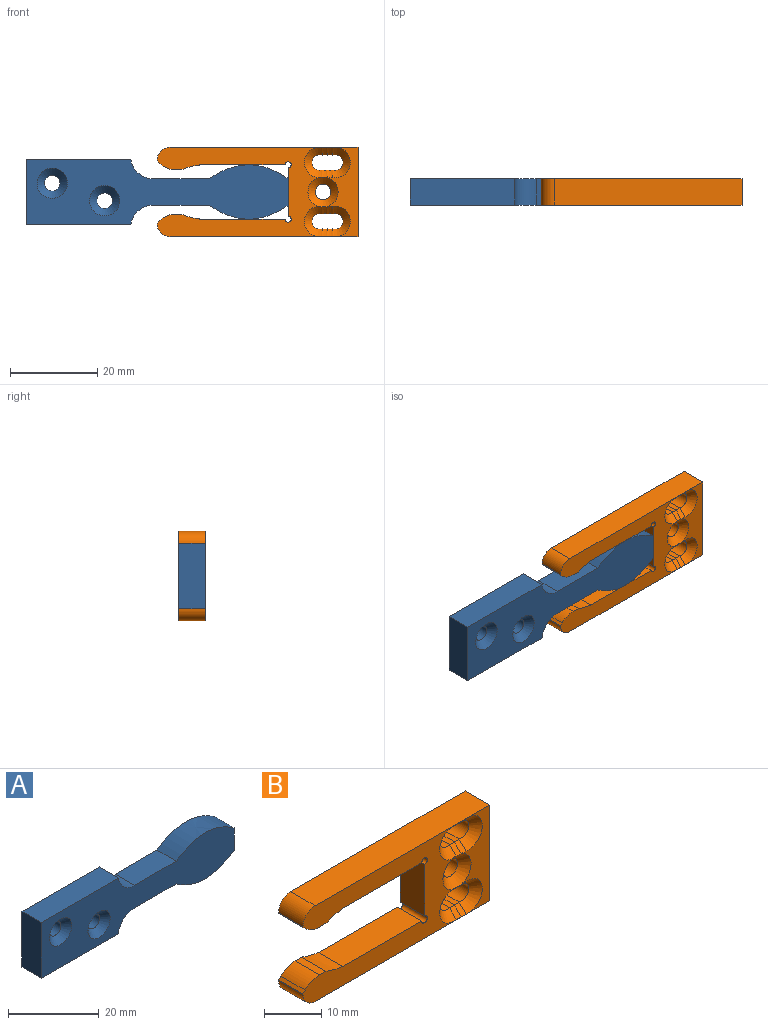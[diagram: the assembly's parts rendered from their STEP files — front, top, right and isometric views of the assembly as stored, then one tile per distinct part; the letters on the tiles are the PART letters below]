
ASSEMBLY  parts=2 mates=1
PART A: 16 faces, bbox 60x6x15 mm
  f0: plane 13.03x6mm, normal (0,0,-1), area 78.2mm2, adj f1,f8,f9,f10
  f1: extruded ~18x6mm, area 116.3mm2, adj f0,f2,f8,f9
  f2: plane 6.11x6mm, normal (1,0,0), area 36.7mm2, adj f1,f3,f8,f9
  f3: extruded ~18x6mm, area 116.3mm2, adj f2,f4,f8,f9
  f4: plane 13.03x6mm, normal (0,0,1), area 78.2mm2, adj f3,f8,f9,f11
  f5: plane 24x6mm, normal (0,0,1), area 144mm2, adj f6,f8,f9,f11
  f6: plane 15x6mm, normal (-1,0,0), area 90mm2, adj f5,f7,f8,f9
  f7: plane 24x6mm, normal (0,0,-1), area 144mm2, adj f6,f8,f9,f10
  f8: plane 60x15mm, normal (0,1,0), area 646.1mm2, adj f0,f1,f2,f3,f4,f5,f6,f7
  f9: plane 60x15mm, normal (0,-1,0), area 590.8mm2, adj f0,f1,f2,f3,f4,f5,f6,f7
  f10: cylinder r=5mm len=6mm, axis (0,-1,0), area 43.8mm2, adj f0,f7,f8,f9
  f11: cylinder r=5mm len=6mm, axis (0,-1,0), area 43.8mm2, adj f4,f5,f8,f9
  f12: cylinder r=1.8mm len=4.33mm, axis (0,-1,0), area 49mm2, adj f8,f13
  f13: cone r=1.8mm half-angle=45deg, axis (0,-1,0), area 39.1mm2, adj f9,f12
  f14: cylinder r=1.8mm len=4.33mm, axis (0,-1,0), area 49mm2, adj f8,f15
  f15: cone r=1.8mm half-angle=45deg, axis (0,-1,0), area 39.1mm2, adj f9,f14
PART B: 50 faces, bbox 46x6x20.4 mm
  f0: plane 46x20.43mm, normal (0,-1,0), area 409.2mm2, adj f1,f2,f4,f5,f6,f7,f8,f9
  f1: plane 6x0.06mm, normal (1,0,0), area 0.3mm2, adj f0,f3,f11,f16
  f2: plane 6x1.62mm, normal (0,0,1), area 9.7mm2, adj f0,f3,f16,f23
  f3: plane 46x20.43mm, normal (0,1,0), area 515.9mm2, adj f1,f2,f4,f5,f6,f7,f8,f9
  f4: plane 6x0.1mm, normal (-1,0,0), area 0.6mm2, adj f0,f3,f18,f21
  f5: plane 6x1.62mm, normal (0,0,-1), area 9.7mm2, adj f0,f3,f17,f22
  f6: plane 6x0.06mm, normal (1,0,0), area 0.3mm2, adj f0,f3,f7,f17
  f7: plane 19.5x6mm, normal (0,0,-1), area 117mm2, adj f0,f3,f6,f8
  f8: cylinder r=0.7mm len=6mm, axis (0,-1,0), area 19.8mm2, adj f0,f3,f7,f9
  f9: plane 11.04x6mm, normal (-1,0,0), area 66.2mm2, adj f0,f3,f8,f10
  f10: cylinder r=0.7mm len=6mm, axis (0,-1,0), area 19.8mm2, adj f0,f3,f9,f11
  f11: plane 19.5x6mm, normal (0,0,1), area 117mm2, adj f0,f1,f3,f10
  f12: plane 6x0.1mm, normal (-1,0,0), area 0.6mm2, adj f0,f3,f19,f20
  f13: plane 43x6mm, normal (0,0,-1), area 258mm2, adj f0,f3,f14,f19
  f14: plane 20.43x6mm, normal (1,0,0), area 122.6mm2, adj f0,f3,f13,f15
  f15: plane 43x6mm, normal (0,0,1), area 258mm2, adj f0,f3,f14,f18
  f16: extruded ~6x4.11mm, area 25.5mm2, adj f0,f1,f2,f3
  f17: extruded ~6x4.11mm, area 25.5mm2, adj f0,f3,f5,f6
  f18: cylinder r=3mm len=6mm, axis (0,-1,0), area 28.3mm2, adj f0,f3,f4,f15
  f19: cylinder r=3mm len=6mm, axis (0,-1,0), area 28.3mm2, adj f0,f3,f12,f13
  f20: plane 6x0.54mm, normal (-0.71,0,0.71), area 4.5mm2, adj f0,f3,f12,f23
  f21: plane 6x0.54mm, normal (-0.71,0,-0.71), area 4.5mm2, adj f0,f3,f4,f22
  f22: cylinder r=5mm len=6mm, axis (0,1,0), area 23.6mm2, adj f0,f3,f5,f21
  f23: cylinder r=5mm len=6mm, axis (0,1,0), area 23.6mm2, adj f0,f2,f3,f20
  f24: cylinder r=1.8mm len=4.33mm, axis (0,-1,0), area 29.8mm2, adj f3,f25,f26,f37
  f25: cylinder r=1.8mm len=4.33mm, axis (0,-1,0), area 5.3mm2, adj f3,f24,f27,f38
  f26: cylinder r=1.8mm len=4.33mm, axis (0,-1,0), area 5.3mm2, adj f3,f24,f28,f39
  f27: cylinder r=1.8mm len=4.33mm, axis (0,-1,0), area 5.3mm2, adj f3,f25,f29,f42
  f28: cylinder r=1.8mm len=4.33mm, axis (0,-1,0), area 5.3mm2, adj f3,f26,f29,f41
  f29: cylinder r=1.8mm len=4.33mm, axis (0,-1,0), area 29.8mm2, adj f3,f27,f28,f43
  f30: cylinder r=1.8mm len=4.33mm, axis (0,-1,0), area 5.3mm2, adj f3,f32,f36,f44
  f31: cylinder r=1.8mm len=4.33mm, axis (0,-1,0), area 5.3mm2, adj f3,f33,f36,f45
  f32: cylinder r=1.8mm len=4.33mm, axis (0,-1,0), area 5.3mm2, adj f3,f30,f34,f46
  f33: cylinder r=1.8mm len=4.33mm, axis (0,-1,0), area 5.3mm2, adj f3,f31,f34,f47
  f34: cylinder r=1.8mm len=4.33mm, axis (0,-1,0), area 29.8mm2, adj f3,f32,f33,f48
  f35: cylinder r=1.8mm len=4.33mm, axis (0,-1,0), area 49mm2, adj f3,f40
  f36: cylinder r=1.8mm len=4.33mm, axis (0,-1,0), area 29.8mm2, adj f3,f30,f31,f49
  f37: cone r=1.8mm half-angle=45deg, axis (0,-1,0), area 22.6mm2, adj f0,f24,f38,f39,f40
  f38: cone r=1.8mm half-angle=45deg, axis (0,-1,0), area 3.1mm2, adj f0,f25,f37,f42
  f39: cone r=1.8mm half-angle=45deg, axis (0,-1,0), area 3mm2, adj f26,f37,f40,f41
  f40: cone r=1.8mm half-angle=45deg, axis (0,-1,0), area 38.7mm2, adj f0,f35,f37,f39,f41,f44,f46,f49
  f41: cone r=1.8mm half-angle=45deg, axis (0,-1,0), area 2.9mm2, adj f0,f28,f39,f40,f43
  f42: cone r=1.8mm half-angle=45deg, axis (0,-1,0), area 3.1mm2, adj f0,f27,f38,f43
  f43: cone r=1.8mm half-angle=45deg, axis (0,-1,0), area 22.6mm2, adj f0,f29,f41,f42
  f44: cone r=1.8mm half-angle=45deg, axis (0,-1,0), area 3mm2, adj f30,f40,f46,f49
  f45: cone r=1.8mm half-angle=45deg, axis (0,-1,0), area 3.1mm2, adj f0,f31,f47,f49
  f46: cone r=1.8mm half-angle=45deg, axis (0,-1,0), area 2.9mm2, adj f0,f32,f40,f44,f48
  f47: cone r=1.8mm half-angle=45deg, axis (0,-1,0), area 3.1mm2, adj f0,f33,f45,f48
  f48: cone r=1.8mm half-angle=45deg, axis (0,-1,0), area 22.6mm2, adj f0,f34,f46,f47
  f49: cone r=1.8mm half-angle=45deg, axis (0,-1,0), area 22.6mm2, adj f0,f36,f40,f44,f45
PLACE A t=(-9.71,4.84,-5.81)mm fixed
PLACE B t=(-19.71,4.84,-5.81)mm
MATE slider B.f9 <-> A.f2  axis (-1,0,0) through (38.29,7.84,-5.81)mm
